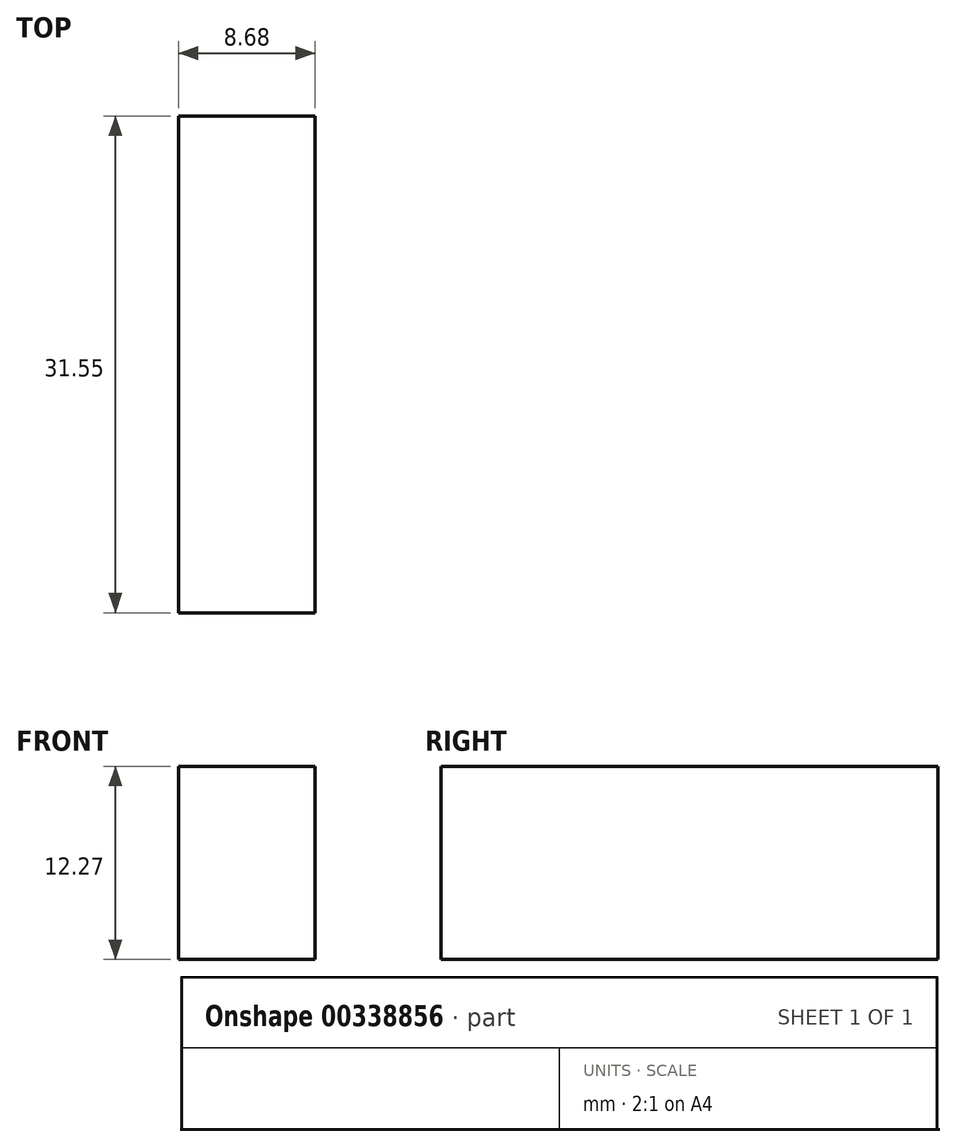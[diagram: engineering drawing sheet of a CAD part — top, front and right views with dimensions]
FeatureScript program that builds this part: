
annotation { "Feature Type Name" : "Feature", "Feature Type Description" : "" }
export const myFeature = defineFeature(function(context is Context, id is Id, definition is map)
    precondition{}
    {
        {
            var Q0;
            Q0=qCreatedBy(makeId("Front.planeOp"),FACE);
            var sketch = newSketch(context, id + "F0", { "sketchPlane" : qUnion([Q0])});
            skLineSegment(sketch, "E0.bottom", {"start": v(-5.11, 3.56) * mm, "end": v(3.57, 3.56) * mm});
            skLineSegment(sketch, "E0.top", {"start": v(-5.11, -8.7) * mm, "end": v(3.57, -8.7) * mm});
            skLineSegment(sketch, "E0.left", {"start": v(-5.11, 3.56) * mm, "end": v(-5.11, -8.7) * mm});
            skLineSegment(sketch, "E0.right", {"start": v(3.57, 3.56) * mm, "end": v(3.57, -8.7) * mm});
            skSolve(sketch);
        }
        {
            var Q0;
            Q0 = qSketchRegion(id + "F0", true);
            extrude(context, id + "F1", {"entities" : qUnion([Q0]), "depth" : 31.55 * mm});
        }
    });
